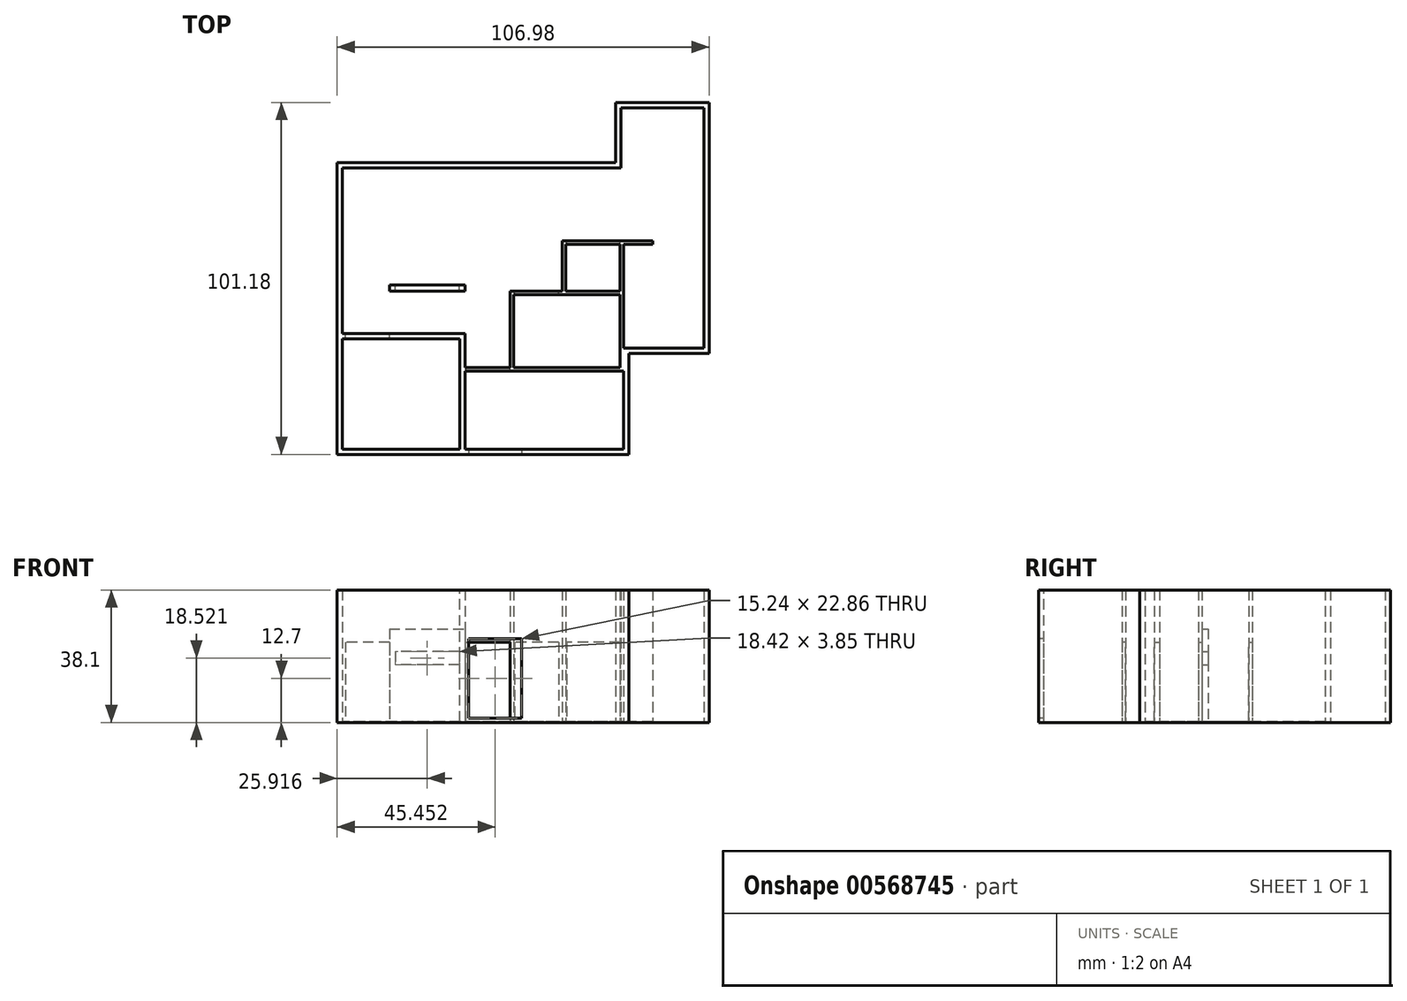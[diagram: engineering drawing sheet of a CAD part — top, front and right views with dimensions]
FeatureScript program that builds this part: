
annotation { "Feature Type Name" : "Feature", "Feature Type Description" : "" }
export const myFeature = defineFeature(function(context is Context, id is Id, definition is map)
    precondition{}
    {
        {
            var Q0;
            Q0=qCreatedBy(makeId("Top.planeOp"),FACE);
            var sketch = newSketch(context, id + "F0", { "sketchPlane" : qUnion([Q0])});
            skLineSegment(sketch, "E0.bottom", {"start": v(42.29, -41.97) * mm, "end": v(-41.64, -41.97) * mm});
            skLineSegment(sketch, "E0.top", {"start": v(42.29, 41.96) * mm, "end": v(-41.64, 41.96) * mm});
            skLineSegment(sketch, "E0.left", {"start": v(42.29, -41.97) * mm, "end": v(42.29, 41.96) * mm});
            skLineSegment(sketch, "E0.right", {"start": v(-41.64, -41.97) * mm, "end": v(-41.64, 41.96) * mm});
            skPoint(sketch, "E0.middle", {"position": v(0.32, 0) * mm});
            skLineSegment(sketch, "E1.MirrorCS", {"start": v(59.54, -38.2) * mm, "end": v(59.54, -65.02) * mm});
            skLineSegment(sketch, "E2.MirrorCS", {"start": v(-12.63, -38.2) * mm, "end": v(-12.63, -65.02) * mm});
            skPoint(sketch, "E3.MirrorP", {"position": v(-0.32, 0) * mm});
            skLineSegment(sketch, "E4.MirrorCS", {"start": v(-12.63, -65.02) * mm, "end": v(59.54, -65.02) * mm});
            skLineSegment(sketch, "E5.MirrorCS", {"start": v(-12.63, -38.2) * mm, "end": v(59.54, -38.2) * mm});
            skSolve(sketch);
        }
        {
            var Q0;
            {var subQ2=sQuery(id+"F0.wireOp",EDGE,"E0.top");Q0=makeQuery(id+"F0.imprint","IMPRINT",FACE,{"disambiguationData":[TD([[makeQuery(id+"F0.imprint","IMPRINT",EDGE,{"derivedFrom":subQ2}),1.0]])]});}
            var Q1;
            {var subQ0=sQuery(id+"F0.wireOp",EDGE,"E1.MirrorCS");Q1=makeQuery(id+"F0.imprint","IMPRINT",FACE,{"disambiguationData":[TD([[makeQuery(id+"F0.imprint","IMPRINT",EDGE,{"derivedFrom":subQ0}),-1.0]])]});}
            var Q2;
            {var subQ0=sQuery(id+"F0.wireOp",EDGE,"E0.left");var subQ1=sQuery(id+"F0.wireOp",EDGE,"E0.bottom");var subQ2=makeQuery(id+"F0.imprint","INTERSECT",VERTEX,{"derivedFrom":[subQ1,subQ0]});Q2=makeQuery(id+"F0.imprint","IMPRINT",FACE,{"disambiguationData":[TD([[makeQuery(id+"F0.imprint","IMPRINT",EDGE,{"disambiguationData":[TD([[subQ2,-1.0]])],"derivedFrom":subQ1}),-1.0]])]});}
            extrude(context, id + "F1", {"entities" : qUnion([Q0, Q1, Q2]), "depth" : 38.1 * mm, "offsetDistance" : 25.4 * mm});
        }
        {
            var Q0;
            Q0=makeQuery(id+"F1.opExtrude","CAP_FACE",FACE,{"disambiguationData":[OSD([sQuery(id+"F0.wireOp",EDGE,"E0.bottom"),sQuery(id+"F0.wireOp",EDGE,"E0.top"),sQuery(id+"F0.wireOp",EDGE,"E0.left"),sQuery(id+"F0.wireOp",EDGE,"E0.right"),sQuery(id+"F0.wireOp",EDGE,"E1.MirrorCS"),sQuery(id+"F0.wireOp",EDGE,"E2.MirrorCS"),sQuery(id+"F0.wireOp",EDGE,"E4.MirrorCS"),sQuery(id+"F0.wireOp",EDGE,"E5.MirrorCS")])],"isStart":false});
            shell(context, id + "F2", {"entities" : qUnion([Q0]), "thickness" : 1.52 * mm});
        }
        {
            var Q0;
            Q0=makeQuery(id+"F1.opExtrude","SWEPT_BODY",BODY,{"disambiguationData":[OSD([sQuery(id+"F0.wireOp",EDGE,"E0.bottom"),sQuery(id+"F0.wireOp",EDGE,"E0.top"),sQuery(id+"F0.wireOp",EDGE,"E0.left"),sQuery(id+"F0.wireOp",EDGE,"E0.right"),sQuery(id+"F0.wireOp",EDGE,"E1.MirrorCS"),sQuery(id+"F0.wireOp",EDGE,"E2.MirrorCS"),sQuery(id+"F0.wireOp",EDGE,"E4.MirrorCS"),sQuery(id+"F0.wireOp",EDGE,"E5.MirrorCS")])]});
            var Q1;
            Q1=makeQuery(id+"F1.opExtrude","SWEPT_EDGE",EDGE,{"disambiguationData":[OSD([sQuery(id+"F0.wireOp",EDGE,"E2.MirrorCS"),sQuery(id+"F0.wireOp",EDGE,"E4.MirrorCS")])]});
            transform(context, id + "F3", {"entities" : qUnion([Q0]), "transformType" : TransformType.ROTATION, "transformAxis" : qUnion([Q1]), "angle" : 270 * degree, "makeCopy" : false});
        }
        {
            var Q0;
            Q0=makeQuery(id+"F1.opExtrude","SWEPT_BODY",BODY,{"disambiguationData":[OSD([sQuery(id+"F0.wireOp",EDGE,"E0.bottom"),sQuery(id+"F0.wireOp",EDGE,"E0.top"),sQuery(id+"F0.wireOp",EDGE,"E0.left"),sQuery(id+"F0.wireOp",EDGE,"E0.right"),sQuery(id+"F0.wireOp",EDGE,"E1.MirrorCS"),sQuery(id+"F0.wireOp",EDGE,"E2.MirrorCS"),sQuery(id+"F0.wireOp",EDGE,"E4.MirrorCS"),sQuery(id+"F0.wireOp",EDGE,"E5.MirrorCS")])]});
            transform(context, id + "F4", {"entities" : qUnion([Q0]), "transformType" : TransformType.TRANSLATION_3D, "dx" : 77.47 * mm, "dy" : 55.37 * mm, "dz" : 0 * mm, "makeCopy" : false});
        }
        {
            var Q0;
            Q0=makeQuery(id+"F2.opShell","OFFSET_FACE",FACE,{"disambiguationData":[OSD([sQuery(id+"F0.wireOp",EDGE,"E0.bottom"),sQuery(id+"F0.wireOp",EDGE,"E0.top"),sQuery(id+"F0.wireOp",EDGE,"E0.left"),sQuery(id+"F0.wireOp",EDGE,"E0.right"),sQuery(id+"F0.wireOp",EDGE,"E1.MirrorCS"),sQuery(id+"F0.wireOp",EDGE,"E2.MirrorCS"),sQuery(id+"F0.wireOp",EDGE,"E4.MirrorCS"),sQuery(id+"F0.wireOp",EDGE,"E5.MirrorCS")])]});
            var sketch = newSketch(context, id + "F5", { "sketchPlane" : qUnion([Q0])});
            skLineSegment(sketch, "E6", {"start": v(40.26, 22.82) * mm, "end": v(40.26, -13.72) * mm});
            skLineSegment(sketch, "E7", {"start": v(43.34, 22.82) * mm, "end": v(40.26, 22.82) * mm});
            skLineSegment(sketch, "E8", {"start": v(38.23, -13.72) * mm, "end": v(-5.32, -13.72) * mm});
            skLineSegment(sketch, "E9", {"start": v(-8.67, -37.13) * mm, "end": v(-8.67, -8.13) * mm});
            skLineSegment(sketch, "E10", {"start": v(7.55, -13.72) * mm, "end": v(7.55, 8.33) * mm});
            skLineSegment(sketch, "E11", {"start": v(7.55, 8.33) * mm, "end": v(40.26, 8.33) * mm});
            skLineSegment(sketch, "E12", {"start": v(40.26, 22.82) * mm, "end": v(22.55, 22.82) * mm});
            skLineSegment(sketch, "E13", {"start": v(22.55, 22.82) * mm, "end": v(22.55, 8.33) * mm});
            skLineSegment(sketch, "E14", {"start": v(-5.32, -13.72) * mm, "end": v(-5.32, -3.92) * mm});
            skLineSegment(sketch, "E15", {"start": v(-5.32, -3.92) * mm, "end": v(-40.62, -3.92) * mm});
            skLineSegment(sketch, "E16", {"start": v(-30.23, 9.32) * mm, "end": v(-5.32, 9.32) * mm});
            skSolve(sketch);
        }
        {
            var Q0;
            {var subQ0=sQuery(id+"F5.wireOp",EDGE,"E12");Q0=makeQuery(id+"F5.imprint","IMPRINT",FACE,{"disambiguationData":[TD([[makeQuery(id+"F5.imprint","IMPRINT",EDGE,{"derivedFrom":subQ0}),1.0]])]});}
            var Q1;
            {var subQ6=sQuery(id+"F5.wireOp",EDGE,"E10");Q1=makeQuery(id+"F5.imprint","IMPRINT",FACE,{"disambiguationData":[TD([[makeQuery(id+"F5.imprint","IMPRINT",EDGE,{"derivedFrom":subQ6}),-1.0]])]});}
            var Q2;
            {var subQ1=sQuery(id+"F5.wireOp",EDGE,"E14");Q2=makeQuery(id+"F5.imprint","IMPRINT",FACE,{"disambiguationData":[TD([[makeQuery(id+"F5.imprint","IMPRINT",EDGE,{"derivedFrom":subQ1}),1.0]])]});}
            extrude(context, id + "F6", {"entities" : qUnion([Q0, Q1, Q2]), "operationType" : NewBodyOperationType.ADD, "depth" : 25.4 * mm, "offsetDistance" : 25.4 * mm});
        }
        {
            var Q0;
            Q0=makeQuery(id+"F6.opExtrude","CAP_FACE",FACE,{"disambiguationData":[OSD([sQuery(id+"F0.wireOp",EDGE,"E0.bottom"),sQuery(id+"F0.wireOp",EDGE,"E0.top"),sQuery(id+"F0.wireOp",EDGE,"E0.right"),sQuery(id+"F5.wireOp",EDGE,"E6"),sQuery(id+"F5.wireOp",EDGE,"E8"),sQuery(id+"F5.wireOp",EDGE,"E10"),sQuery(id+"F5.wireOp",EDGE,"E11"),sQuery(id+"F5.wireOp",EDGE,"E12"),sQuery(id+"F5.wireOp",EDGE,"E13"),sQuery(id+"F5.wireOp",EDGE,"E14"),sQuery(id+"F5.wireOp",EDGE,"E15")])],"isStart":false});
            shell(context, id + "F7", {"entities" : qUnion([Q0]), "thickness" : 1.02 * mm});
        }
        {
            var Q0;
            Q0=makeQuery(id+"F7.opShell","OFFSET_FACE",FACE,{"disambiguationData":[OSD([sQuery(id+"F0.wireOp",EDGE,"E0.bottom"),sQuery(id+"F0.wireOp",EDGE,"E0.top"),sQuery(id+"F0.wireOp",EDGE,"E0.left"),sQuery(id+"F0.wireOp",EDGE,"E0.right"),sQuery(id+"F0.wireOp",EDGE,"E1.MirrorCS"),sQuery(id+"F0.wireOp",EDGE,"E2.MirrorCS"),sQuery(id+"F0.wireOp",EDGE,"E4.MirrorCS"),sQuery(id+"F0.wireOp",EDGE,"E5.MirrorCS")])]});
            var sketch = newSketch(context, id + "F8", { "sketchPlane" : qUnion([Q0])});
            skLineSegment(sketch, "E17.bottom", {"start": v(-6.34, -14.74) * mm, "end": v(-5.32, -14.74) * mm});
            skLineSegment(sketch, "E17.top", {"start": v(-6.34, -37.64) * mm, "end": v(-5.32, -37.64) * mm});
            skLineSegment(sketch, "E17.left", {"start": v(-6.34, -14.74) * mm, "end": v(-6.34, -37.64) * mm});
            skLineSegment(sketch, "E17.right", {"start": v(-5.32, -14.74) * mm, "end": v(-5.32, -37.64) * mm});
            skLineSegment(sketch, "E18.bottom", {"start": v(8.56, -14.74) * mm, "end": v(40.26, -14.74) * mm});
            skLineSegment(sketch, "E18.top", {"start": v(8.56, -13.72) * mm, "end": v(40.26, -13.72) * mm});
            skLineSegment(sketch, "E18.left", {"start": v(8.56, -14.74) * mm, "end": v(8.56, -13.72) * mm});
            skLineSegment(sketch, "E18.right", {"start": v(40.26, -14.74) * mm, "end": v(40.26, -13.72) * mm});
            skLineSegment(sketch, "E19.bottom", {"start": v(23.56, 7.32) * mm, "end": v(39.25, 7.32) * mm});
            skLineSegment(sketch, "E19.top", {"start": v(23.56, 8.33) * mm, "end": v(39.25, 8.33) * mm});
            skLineSegment(sketch, "E19.left", {"start": v(23.56, 7.32) * mm, "end": v(23.56, 8.33) * mm});
            skLineSegment(sketch, "E19.right", {"start": v(39.25, 7.32) * mm, "end": v(39.25, 8.33) * mm});
            skLineSegment(sketch, "E20.bottom", {"start": v(40.26, 22.82) * mm, "end": v(48.56, 22.82) * mm});
            skLineSegment(sketch, "E20.top", {"start": v(40.26, 21.8) * mm, "end": v(48.56, 21.8) * mm});
            skLineSegment(sketch, "E20.left", {"start": v(40.26, 22.82) * mm, "end": v(40.26, 21.8) * mm});
            skLineSegment(sketch, "E20.right", {"start": v(48.56, 22.82) * mm, "end": v(48.56, 21.8) * mm});
            skLineSegment(sketch, "E21.bottom", {"start": v(40.26, -13.72) * mm, "end": v(39.25, -13.72) * mm});
            skLineSegment(sketch, "E21.top", {"start": v(40.26, -9.14) * mm, "end": v(39.25, -9.14) * mm});
            skLineSegment(sketch, "E21.left", {"start": v(40.26, -13.72) * mm, "end": v(40.26, -9.14) * mm});
            skLineSegment(sketch, "E21.right", {"start": v(39.25, -13.72) * mm, "end": v(39.25, -9.14) * mm});
            skSolve(sketch);
        }
        {
            var Q0;
            Q0=makeQuery(id+"F7.opShell","OFFSET_FACE",FACE,{"disambiguationData":[OSD([sQuery(id+"F0.wireOp",EDGE,"E0.bottom")])]});
            var Q1;
            Q1=makeQuery(id+"F2.opShell","OFFSET_FACE",FACE,{"disambiguationData":[OSD([sQuery(id+"F0.wireOp",EDGE,"E0.bottom")])]});
            extrude(context, id + "F9", {"entities" : qUnion([Q0]), "operationType" : NewBodyOperationType.ADD, "endBound" : BoundingType.UP_TO_SURFACE, "depth" : 25.4 * mm, "endBoundEntityFace" : qUnion([Q1]), "offsetDistance" : 25.4 * mm});
        }
        {
            var Q0;
            Q0=makeQuery(id+"F7.opShell","OFFSET_FACE",FACE,{"disambiguationData":[OSD([sQuery(id+"F0.wireOp",EDGE,"E0.right")])]});
            var Q1;
            Q1=makeQuery(id+"F2.opShell","OFFSET_FACE",FACE,{"disambiguationData":[OSD([sQuery(id+"F0.wireOp",EDGE,"E0.right")])]});
            extrude(context, id + "F10", {"entities" : qUnion([Q0]), "operationType" : NewBodyOperationType.ADD, "endBound" : BoundingType.UP_TO_SURFACE, "depth" : 25.4 * mm, "endBoundEntityFace" : qUnion([Q1]), "offsetDistance" : 25.4 * mm});
        }
        {
            var Q0;
            Q0=makeQuery(id+"F7.opShell","OFFSET_FACE",FACE,{"disambiguationData":[OSD([sQuery(id+"F0.wireOp",EDGE,"E0.top")])]});
            var Q1;
            Q1=makeQuery(id+"F2.opShell","OFFSET_FACE",FACE,{"disambiguationData":[OSD([sQuery(id+"F0.wireOp",EDGE,"E0.top")])]});
            extrude(context, id + "F11", {"entities" : qUnion([Q0]), "operationType" : NewBodyOperationType.ADD, "endBound" : BoundingType.UP_TO_SURFACE, "depth" : 25.4 * mm, "endBoundEntityFace" : qUnion([Q1]), "offsetDistance" : 25.4 * mm});
        }
        {
            var Q0;
            Q0 = qSketchRegion(id + "F8", true);
            var Q1;
            Q1=makeQuery(id+"F6.opExtrude","CAP_FACE",FACE,{"disambiguationData":[OSD([sQuery(id+"F0.wireOp",EDGE,"E0.bottom"),sQuery(id+"F0.wireOp",EDGE,"E0.top"),sQuery(id+"F0.wireOp",EDGE,"E0.right"),sQuery(id+"F5.wireOp",EDGE,"E6"),sQuery(id+"F5.wireOp",EDGE,"E8"),sQuery(id+"F5.wireOp",EDGE,"E10"),sQuery(id+"F5.wireOp",EDGE,"E11"),sQuery(id+"F5.wireOp",EDGE,"E12"),sQuery(id+"F5.wireOp",EDGE,"E13"),sQuery(id+"F5.wireOp",EDGE,"E14"),sQuery(id+"F5.wireOp",EDGE,"E15")])],"isStart":false});
            extrude(context, id + "F12", {"entities" : qUnion([Q0]), "operationType" : NewBodyOperationType.ADD, "endBound" : BoundingType.UP_TO_SURFACE, "depth" : 26.67 * mm, "endBoundEntityFace" : qUnion([Q1]), "offsetDistance" : 25.4 * mm});
        }
        {
            var Q0;
            Q0=makeQuery(id+"F7.opShell","OFFSET_FACE",FACE,{"disambiguationData":[OSD([sQuery(id+"F5.wireOp",EDGE,"E15")])]});
            extrude(context, id + "F13", {"entities" : qUnion([Q0]), "operationType" : NewBodyOperationType.ADD, "depth" : 0.5 * mm, "offsetDistance" : 25.4 * mm});
        }
        {
            var Q0;
            Q0=makeQuery(id+"F12.boolean.opBoolean","MERGE",FACE,{"derivedFrom":[makeQuery(id+"F7.opShell","OFFSET_FACE",FACE,{"disambiguationData":[OSD([sQuery(id+"F5.wireOp",EDGE,"E14")])]}),makeQuery(id+"F12.opExtrude","SWEPT_FACE",FACE,{"disambiguationData":[OSD([sQuery(id+"F8.wireOp",EDGE,"E17.left")])]})]});
            extrude(context, id + "F14", {"entities" : qUnion([Q0]), "operationType" : NewBodyOperationType.ADD, "depth" : 0.5 * mm, "offsetDistance" : 25.4 * mm});
        }
        {
            var Q0;
            Q0=makeQuery(id+"F1.opExtrude","SWEPT_FACE",FACE,{"disambiguationData":[OSD([sQuery(id+"F0.wireOp",EDGE,"E0.right")])]});
            var sketch = newSketch(context, id + "F15", { "sketchPlane" : qUnion([Q0])});
            skLineSegment(sketch, "E22.bottom", {"start": v(-4.3, 1.27) * mm, "end": v(10.93, 1.27) * mm});
            skLineSegment(sketch, "E22.top", {"start": v(-4.3, 24.13) * mm, "end": v(10.93, 24.13) * mm});
            skLineSegment(sketch, "E22.left", {"start": v(-4.3, 1.27) * mm, "end": v(-4.3, 24.13) * mm});
            skLineSegment(sketch, "E22.right", {"start": v(10.93, 1.27) * mm, "end": v(10.93, 24.13) * mm});
            skSolve(sketch);
        }
        {
            var Q0;
            Q0=makeQuery(id+"F15.imprint","IMPRINT",FACE,{"disambiguationData":[TD([[makeQuery(id+"F15.imprint","IMPRINT",EDGE,{"derivedFrom":sQuery(id+"F15.wireOp",EDGE,"E22.bottom")}),1.0]])]});
            extrude(context, id + "F16", {"entities" : qUnion([Q0]), "operationType" : NewBodyOperationType.REMOVE, "oppositeDirection" : true, "depth" : 2.54 * mm, "offsetDistance" : 25.4 * mm});
        }
        {
            var Q0;
            Q0=makeQuery(id+"F2.opShell","OFFSET_FACE",FACE,{"disambiguationData":[OSD([sQuery(id+"F0.wireOp",EDGE,"E0.bottom"),sQuery(id+"F0.wireOp",EDGE,"E0.top"),sQuery(id+"F0.wireOp",EDGE,"E0.left"),sQuery(id+"F0.wireOp",EDGE,"E0.right"),sQuery(id+"F0.wireOp",EDGE,"E1.MirrorCS"),sQuery(id+"F0.wireOp",EDGE,"E2.MirrorCS"),sQuery(id+"F0.wireOp",EDGE,"E4.MirrorCS"),sQuery(id+"F0.wireOp",EDGE,"E5.MirrorCS")])]});
            extrude(context, id + "F17", {"entities" : qUnion([Q0]), "operationType" : NewBodyOperationType.REMOVE, "oppositeDirection" : true, "depth" : 1.27 * mm, "offsetDistance" : 25.4 * mm});
        }
        {
            var Q0;
            {var subQ0=sQuery(id+"F5.wireOp",EDGE,"E11");Q0=makeQuery(id+"F17.boolean.opBoolean","MERGE",FACE,{"derivedFrom":[makeQuery(id+"F6.opExtrude","SWEPT_FACE",FACE,{"disambiguationData":[OSD([subQ0])]}),makeQuery(id+"F17.opExtrude","SWEPT_FACE",FACE,{"disambiguationData":[OSD([subQ0])]})]});}
            var sketch = newSketch(context, id + "F18", { "sketchPlane" : qUnion([Q0])});
            skLineSegment(sketch, "E23.bottom", {"start": v(-21.52, 23.11) * mm, "end": v(-8.82, 23.11) * mm});
            skLineSegment(sketch, "E23.top", {"start": v(-21.52, 0.25) * mm, "end": v(-8.82, 0.25) * mm});
            skLineSegment(sketch, "E23.left", {"start": v(-21.52, 23.11) * mm, "end": v(-21.52, 0.25) * mm});
            skLineSegment(sketch, "E23.right", {"start": v(-8.82, 23.11) * mm, "end": v(-8.82, 0.25) * mm});
            skSolve(sketch);
        }
        {
            var Q0;
            {var subQ0=sQuery(id+"F18.wireOp",EDGE,"E23.bottom");Q0=makeQuery(id+"F18.imprint","IMPRINT",FACE,{"disambiguationData":[TD([[makeQuery(id+"F18.imprint","IMPRINT",EDGE,{"derivedFrom":subQ0}),-1.0]])]});}
            extrude(context, id + "F19", {"entities" : qUnion([Q0]), "operationType" : NewBodyOperationType.REMOVE, "oppositeDirection" : true, "depth" : 1.27 * mm, "offsetDistance" : 25.4 * mm});
        }
        {
            var Q0;
            {var subQ0=sQuery(id+"F8.wireOp",EDGE,"E20.bottom");Q0=makeQuery(id+"F17.boolean.opBoolean","MERGE",FACE,{"derivedFrom":[makeQuery(id+"F12.boolean.opBoolean","MERGE",FACE,{"derivedFrom":[makeQuery(id+"F6.opExtrude","SWEPT_FACE",FACE,{"disambiguationData":[OSD([sQuery(id+"F5.wireOp",EDGE,"E12")])]}),makeQuery(id+"F12.opExtrude","SWEPT_FACE",FACE,{"disambiguationData":[OSD([subQ0])]})]})],"fromTools":[makeQuery(id+"F17.opExtrude","SWEPT_FACE",FACE,{"disambiguationData":[OSD([sQuery(id+"F0.wireOp",EDGE,"E0.bottom"),sQuery(id+"F0.wireOp",EDGE,"E0.top"),sQuery(id+"F0.wireOp",EDGE,"E0.left"),sQuery(id+"F0.wireOp",EDGE,"E0.right"),sQuery(id+"F0.wireOp",EDGE,"E1.MirrorCS"),sQuery(id+"F0.wireOp",EDGE,"E2.MirrorCS"),sQuery(id+"F0.wireOp",EDGE,"E4.MirrorCS"),sQuery(id+"F0.wireOp",EDGE,"E5.MirrorCS"),subQ0])]})]});}
            var sketch = newSketch(context, id + "F20", { "sketchPlane" : qUnion([Q0])});
            skLineSegment(sketch, "E24.bottom", {"start": v(-39.25, 23.11) * mm, "end": v(-23.82, 23.11) * mm});
            skLineSegment(sketch, "E24.top", {"start": v(-39.25, 0.25) * mm, "end": v(-23.82, 0.25) * mm});
            skLineSegment(sketch, "E24.left", {"start": v(-39.25, 23.11) * mm, "end": v(-39.25, 0.25) * mm});
            skLineSegment(sketch, "E24.right", {"start": v(-23.82, 23.11) * mm, "end": v(-23.82, 0.25) * mm});
            skSolve(sketch);
        }
        {
            var Q0;
            Q0=makeQuery(id+"F20.imprint","IMPRINT",FACE,{"disambiguationData":[TD([[makeQuery(id+"F20.imprint","IMPRINT",EDGE,{"derivedFrom":sQuery(id+"F20.wireOp",EDGE,"E24.bottom")}),-1.0]])]});
            extrude(context, id + "F21", {"entities" : qUnion([Q0]), "operationType" : NewBodyOperationType.REMOVE, "oppositeDirection" : true, "depth" : 1.27 * mm, "offsetDistance" : 25.4 * mm});
        }
        {
            var Q0;
            {var subQ0=sQuery(id+"F5.wireOp",EDGE,"E15");Q0=makeQuery(id+"F17.boolean.opBoolean","MERGE",FACE,{"derivedFrom":[makeQuery(id+"F6.opExtrude","SWEPT_FACE",FACE,{"disambiguationData":[OSD([subQ0])]}),makeQuery(id+"F17.opExtrude","SWEPT_FACE",FACE,{"disambiguationData":[OSD([subQ0])]})]});}
            var sketch = newSketch(context, id + "F22", { "sketchPlane" : qUnion([Q0])});
            skLineSegment(sketch, "E25.bottom", {"start": v(27.12, 23.11) * mm, "end": v(39.82, 23.11) * mm});
            skLineSegment(sketch, "E25.top", {"start": v(27.12, 0.25) * mm, "end": v(39.82, 0.25) * mm});
            skLineSegment(sketch, "E25.left", {"start": v(27.12, 23.11) * mm, "end": v(27.12, 0.25) * mm});
            skLineSegment(sketch, "E25.right", {"start": v(39.82, 23.11) * mm, "end": v(39.82, 0.25) * mm});
            skSolve(sketch);
        }
        {
            var Q0;
            {var subQ0=sQuery(id+"F22.wireOp",EDGE,"E25.left");Q0=makeQuery(id+"F22.imprint","IMPRINT",FACE,{"disambiguationData":[TD([[makeQuery(id+"F22.imprint","IMPRINT",EDGE,{"derivedFrom":subQ0}),1.0]])]});}
            extrude(context, id + "F23", {"entities" : qUnion([Q0]), "operationType" : NewBodyOperationType.REMOVE, "oppositeDirection" : true, "depth" : 1.78 * mm, "offsetDistance" : 25.4 * mm});
        }
        {
            var Q0;
            Q0=makeQuery(id+"F23.boolean.opBoolean","MERGE",FACE,{"derivedFrom":[makeQuery(id+"F21.boolean.opBoolean","MERGE",FACE,{"derivedFrom":[makeQuery(id+"F19.boolean.opBoolean","MERGE",FACE,{"derivedFrom":[makeQuery(id+"F17.boolean.opBoolean","COPY",FACE,{"derivedFrom":makeQuery(id+"F17.opExtrude","CAP_FACE",FACE,{"disambiguationData":[OSD([sQuery(id+"F0.wireOp",EDGE,"E0.bottom"),sQuery(id+"F0.wireOp",EDGE,"E0.top"),sQuery(id+"F0.wireOp",EDGE,"E0.left"),sQuery(id+"F0.wireOp",EDGE,"E0.right"),sQuery(id+"F0.wireOp",EDGE,"E1.MirrorCS"),sQuery(id+"F0.wireOp",EDGE,"E2.MirrorCS"),sQuery(id+"F0.wireOp",EDGE,"E4.MirrorCS"),sQuery(id+"F0.wireOp",EDGE,"E5.MirrorCS")])],"isStart":false})})],"fromTools":[makeQuery(id+"F19.opExtrude","SWEPT_FACE",FACE,{"disambiguationData":[OSD([sQuery(id+"F18.wireOp",EDGE,"E23.top")])]})]})],"fromTools":[makeQuery(id+"F21.opExtrude","SWEPT_FACE",FACE,{"disambiguationData":[OSD([sQuery(id+"F20.wireOp",EDGE,"E24.top")])]})]})],"fromTools":[makeQuery(id+"F23.opExtrude","SWEPT_FACE",FACE,{"disambiguationData":[OSD([sQuery(id+"F22.wireOp",EDGE,"E25.top")])]})]});
            var sketch = newSketch(context, id + "F24", { "sketchPlane" : qUnion([Q0])});
            skLineSegment(sketch, "E26.bottom", {"start": v(-27.12, 8.33) * mm, "end": v(-5.32, 8.33) * mm});
            skLineSegment(sketch, "E26.top", {"start": v(-27.12, 10.11) * mm, "end": v(-5.32, 10.11) * mm});
            skLineSegment(sketch, "E26.left", {"start": v(-27.12, 8.33) * mm, "end": v(-27.12, 10.11) * mm});
            skLineSegment(sketch, "E26.right", {"start": v(-5.32, 8.33) * mm, "end": v(-5.32, 10.11) * mm});
            skSolve(sketch);
        }
        {
            var Q0;
            Q0=makeQuery(id+"F24.imprint","IMPRINT",FACE,{"disambiguationData":[TD([[makeQuery(id+"F24.imprint","IMPRINT",EDGE,{"derivedFrom":sQuery(id+"F24.wireOp",EDGE,"E26.bottom")}),1.0]])]});
            var Q1;
            {var subQ0=sQuery(id+"F8.wireOp",EDGE,"E17.left");var subQ1=sQuery(id+"F5.wireOp",EDGE,"E14");var subQ2=sQuery(id+"F5.wireOp",EDGE,"E15");Q1=makeQuery(id+"F14.boolean.opBoolean","MERGE",FACE,{"derivedFrom":[makeQuery(id+"F13.boolean.opBoolean","MERGE",FACE,{"derivedFrom":[makeQuery(id+"F12.boolean.opBoolean","MERGE",FACE,{"derivedFrom":[makeQuery(id+"F6.opExtrude","CAP_FACE",FACE,{"disambiguationData":[OSD([sQuery(id+"F0.wireOp",EDGE,"E0.bottom"),sQuery(id+"F0.wireOp",EDGE,"E0.top"),sQuery(id+"F0.wireOp",EDGE,"E0.right"),sQuery(id+"F5.wireOp",EDGE,"E6"),sQuery(id+"F5.wireOp",EDGE,"E8"),sQuery(id+"F5.wireOp",EDGE,"E10"),sQuery(id+"F5.wireOp",EDGE,"E11"),sQuery(id+"F5.wireOp",EDGE,"E12"),sQuery(id+"F5.wireOp",EDGE,"E13"),subQ1,subQ2])],"isStart":false}),makeQuery(id+"F12.opExtrude","CAP_FACE",FACE,{"disambiguationData":[OSD([sQuery(id+"F8.wireOp",EDGE,"E17.bottom"),sQuery(id+"F8.wireOp",EDGE,"E17.top"),subQ0,sQuery(id+"F8.wireOp",EDGE,"E17.right")])],"isStart":false}),makeQuery(id+"F12.opExtrude","CAP_FACE",FACE,{"disambiguationData":[OSD([sQuery(id+"F8.wireOp",EDGE,"E18.bottom"),sQuery(id+"F8.wireOp",EDGE,"E18.top"),sQuery(id+"F8.wireOp",EDGE,"E18.left"),sQuery(id+"F8.wireOp",EDGE,"E18.right"),sQuery(id+"F8.wireOp",EDGE,"E21.bottom"),sQuery(id+"F8.wireOp",EDGE,"E21.top"),sQuery(id+"F8.wireOp",EDGE,"E21.left"),sQuery(id+"F8.wireOp",EDGE,"E21.right")])],"isStart":false}),makeQuery(id+"F12.opExtrude","CAP_FACE",FACE,{"disambiguationData":[OSD([sQuery(id+"F8.wireOp",EDGE,"E19.bottom"),sQuery(id+"F8.wireOp",EDGE,"E19.top"),sQuery(id+"F8.wireOp",EDGE,"E19.left"),sQuery(id+"F8.wireOp",EDGE,"E19.right")])],"isStart":false}),makeQuery(id+"F12.opExtrude","CAP_FACE",FACE,{"disambiguationData":[OSD([sQuery(id+"F8.wireOp",EDGE,"E20.bottom"),sQuery(id+"F8.wireOp",EDGE,"E20.top"),sQuery(id+"F8.wireOp",EDGE,"E20.left"),sQuery(id+"F8.wireOp",EDGE,"E20.right")])],"isStart":false})]}),makeQuery(id+"F13.opExtrude","SWEPT_FACE",FACE,{"disambiguationData":[OSD([subQ2])]})]}),makeQuery(id+"F14.opExtrude","SWEPT_FACE",FACE,{"disambiguationData":[OSD([subQ1,subQ0])]})]});}
            extrude(context, id + "F25", {"entities" : qUnion([Q0]), "operationType" : NewBodyOperationType.ADD, "endBound" : BoundingType.UP_TO_SURFACE, "depth" : 25.4 * mm, "endBoundEntityFace" : qUnion([Q1]), "offsetDistance" : 25.4 * mm});
        }
        {
            var Q0;
            Q0=makeQuery(id+"F25.opExtrude","SWEPT_FACE",FACE,{"disambiguationData":[OSD([sQuery(id+"F24.wireOp",EDGE,"E26.top")])]});
            var sketch = newSketch(context, id + "F26", { "sketchPlane" : qUnion([Q0])});
            skLineSegment(sketch, "E27.bottom", {"start": v(7.01, 20.45) * mm, "end": v(25.43, 20.45) * mm});
            skLineSegment(sketch, "E27.top", {"start": v(7.01, 16.6) * mm, "end": v(25.43, 16.6) * mm});
            skLineSegment(sketch, "E27.left", {"start": v(7.01, 20.45) * mm, "end": v(7.01, 16.6) * mm});
            skLineSegment(sketch, "E27.right", {"start": v(25.43, 20.45) * mm, "end": v(25.43, 16.6) * mm});
            skSolve(sketch);
        }
        {
            var Q0;
            Q0=makeQuery(id+"F26.imprint","IMPRINT",FACE,{"disambiguationData":[TD([[makeQuery(id+"F26.imprint","IMPRINT",EDGE,{"derivedFrom":sQuery(id+"F26.wireOp",EDGE,"E27.bottom")}),-1.0]])]});
            extrude(context, id + "F27", {"entities" : qUnion([Q0]), "operationType" : NewBodyOperationType.REMOVE, "oppositeDirection" : true, "depth" : 1.78 * mm, "offsetDistance" : 25.4 * mm});
        }
        {
            var Q0;
            Q0=makeQuery(id+"F12.boolean.opBoolean","MERGE",FACE,{"derivedFrom":[makeQuery(id+"F7.opShell","OFFSET_FACE",FACE,{"disambiguationData":[OSD([sQuery(id+"F5.wireOp",EDGE,"E8")])]}),makeQuery(id+"F12.opExtrude","SWEPT_FACE",FACE,{"disambiguationData":[OSD([sQuery(id+"F8.wireOp",EDGE,"E18.bottom")])]})]});
            var sketch = newSketch(context, id + "F28", { "sketchPlane" : qUnion([Q0])});
            skLineSegment(sketch, "E28.bottom", {"start": v(-5.15, 23.11) * mm, "end": v(7.55, 23.11) * mm});
            skLineSegment(sketch, "E28.top", {"start": v(-5.15, 0.25) * mm, "end": v(7.55, 0.25) * mm});
            skLineSegment(sketch, "E28.left", {"start": v(-5.15, 23.11) * mm, "end": v(-5.15, 0.25) * mm});
            skLineSegment(sketch, "E28.right", {"start": v(7.55, 23.11) * mm, "end": v(7.55, 0.25) * mm});
            skSolve(sketch);
        }
        {
            var Q0;
            Q0=makeQuery(id+"F28.imprint","IMPRINT",FACE,{"disambiguationData":[TD([[makeQuery(id+"F28.imprint","IMPRINT",EDGE,{"derivedFrom":sQuery(id+"F28.wireOp",EDGE,"E28.bottom")}),-1.0]])]});
            var Q1;
            {var subQ0=sQuery(id+"F5.wireOp",EDGE,"E8");Q1=makeQuery(id+"F17.boolean.opBoolean","MERGE",FACE,{"derivedFrom":[makeQuery(id+"F6.opExtrude","SWEPT_FACE",FACE,{"disambiguationData":[OSD([subQ0])]}),makeQuery(id+"F17.opExtrude","SWEPT_FACE",FACE,{"disambiguationData":[OSD([subQ0])]})]});}
            extrude(context, id + "F29", {"entities" : qUnion([Q0]), "operationType" : NewBodyOperationType.REMOVE, "endBound" : BoundingType.UP_TO_SURFACE, "oppositeDirection" : true, "depth" : 25.4 * mm, "endBoundEntityFace" : qUnion([Q1]), "offsetDistance" : 25.4 * mm});
        }
        {
            var Q0;
            {var subQ0=sQuery(id+"F8.wireOp",EDGE,"E17.left");var subQ1=sQuery(id+"F5.wireOp",EDGE,"E14");var subQ2=sQuery(id+"F5.wireOp",EDGE,"E15");Q0=makeQuery(id+"F14.boolean.opBoolean","MERGE",FACE,{"derivedFrom":[makeQuery(id+"F13.boolean.opBoolean","MERGE",FACE,{"derivedFrom":[makeQuery(id+"F12.boolean.opBoolean","MERGE",FACE,{"derivedFrom":[makeQuery(id+"F6.opExtrude","CAP_FACE",FACE,{"disambiguationData":[OSD([sQuery(id+"F0.wireOp",EDGE,"E0.bottom"),sQuery(id+"F0.wireOp",EDGE,"E0.top"),sQuery(id+"F0.wireOp",EDGE,"E0.right"),sQuery(id+"F5.wireOp",EDGE,"E6"),sQuery(id+"F5.wireOp",EDGE,"E8"),sQuery(id+"F5.wireOp",EDGE,"E10"),sQuery(id+"F5.wireOp",EDGE,"E11"),sQuery(id+"F5.wireOp",EDGE,"E12"),sQuery(id+"F5.wireOp",EDGE,"E13"),subQ1,subQ2])],"isStart":false}),makeQuery(id+"F12.opExtrude","CAP_FACE",FACE,{"disambiguationData":[OSD([sQuery(id+"F8.wireOp",EDGE,"E17.bottom"),sQuery(id+"F8.wireOp",EDGE,"E17.top"),subQ0,sQuery(id+"F8.wireOp",EDGE,"E17.right")])],"isStart":false}),makeQuery(id+"F12.opExtrude","CAP_FACE",FACE,{"disambiguationData":[OSD([sQuery(id+"F8.wireOp",EDGE,"E18.bottom"),sQuery(id+"F8.wireOp",EDGE,"E18.top"),sQuery(id+"F8.wireOp",EDGE,"E18.left"),sQuery(id+"F8.wireOp",EDGE,"E18.right"),sQuery(id+"F8.wireOp",EDGE,"E21.bottom"),sQuery(id+"F8.wireOp",EDGE,"E21.top"),sQuery(id+"F8.wireOp",EDGE,"E21.left"),sQuery(id+"F8.wireOp",EDGE,"E21.right")])],"isStart":false}),makeQuery(id+"F12.opExtrude","CAP_FACE",FACE,{"disambiguationData":[OSD([sQuery(id+"F8.wireOp",EDGE,"E19.bottom"),sQuery(id+"F8.wireOp",EDGE,"E19.top"),sQuery(id+"F8.wireOp",EDGE,"E19.left"),sQuery(id+"F8.wireOp",EDGE,"E19.right")])],"isStart":false}),makeQuery(id+"F12.opExtrude","CAP_FACE",FACE,{"disambiguationData":[OSD([sQuery(id+"F8.wireOp",EDGE,"E20.bottom"),sQuery(id+"F8.wireOp",EDGE,"E20.top"),sQuery(id+"F8.wireOp",EDGE,"E20.left"),sQuery(id+"F8.wireOp",EDGE,"E20.right")])],"isStart":false})]}),makeQuery(id+"F13.opExtrude","SWEPT_FACE",FACE,{"disambiguationData":[OSD([subQ2])]})]}),makeQuery(id+"F14.opExtrude","SWEPT_FACE",FACE,{"disambiguationData":[OSD([subQ1,subQ0])]})]});}
            var Q1;
            Q1=makeQuery(id+"F1.opExtrude","CAP_FACE",FACE,{"disambiguationData":[OSD([sQuery(id+"F0.wireOp",EDGE,"E0.bottom"),sQuery(id+"F0.wireOp",EDGE,"E0.top"),sQuery(id+"F0.wireOp",EDGE,"E0.left"),sQuery(id+"F0.wireOp",EDGE,"E0.right"),sQuery(id+"F0.wireOp",EDGE,"E1.MirrorCS"),sQuery(id+"F0.wireOp",EDGE,"E2.MirrorCS"),sQuery(id+"F0.wireOp",EDGE,"E4.MirrorCS"),sQuery(id+"F0.wireOp",EDGE,"E5.MirrorCS")])],"isStart":false});
            extrude(context, id + "F30", {"entities" : qUnion([Q0]), "operationType" : NewBodyOperationType.ADD, "endBound" : BoundingType.UP_TO_SURFACE, "depth" : 25.4 * mm, "endBoundEntityFace" : qUnion([Q1]), "offsetDistance" : 25.4 * mm});
        }
        {
            var Q0;
            {var subQ0=sQuery(id+"F8.wireOp",EDGE,"E18.right");Q0=makeQuery(id+"F30.boolean.opBoolean","MERGE",FACE,{"derivedFrom":[makeQuery(id+"F12.opExtrude","SWEPT_FACE",FACE,{"disambiguationData":[OSD([subQ0])]}),makeQuery(id+"F30.opExtrude","SWEPT_FACE",FACE,{"disambiguationData":[OSD([subQ0])]})]});}
            var Q1;
            {var subQ0=sQuery(id+"F0.wireOp",EDGE,"E0.bottom");Q1=makeQuery(id+"F9.boolean.opBoolean","MERGE",FACE,{"derivedFrom":[makeQuery(id+"F2.opShell","OFFSET_FACE",FACE,{"disambiguationData":[OSD([subQ0])]}),makeQuery(id+"F9.opExtrude","CAP_FACE",FACE,{"disambiguationData":[OSD([subQ0])],"isStart":false})]});}
            extrude(context, id + "F31", {"entities" : qUnion([Q0]), "operationType" : NewBodyOperationType.ADD, "endBound" : BoundingType.UP_TO_SURFACE, "depth" : 25.4 * mm, "endBoundEntityFace" : qUnion([Q1]), "offsetDistance" : 25.4 * mm});
        }
        {
            var Q0;
            {var subQ0=sQuery(id+"F8.wireOp",EDGE,"E18.bottom");var subQ1=sQuery(id+"F5.wireOp",EDGE,"E8");var subQ2=sQuery(id+"F0.wireOp",EDGE,"E5.MirrorCS");var subQ3=sQuery(id+"F0.wireOp",EDGE,"E4.MirrorCS");var subQ4=sQuery(id+"F0.wireOp",EDGE,"E2.MirrorCS");var subQ5=sQuery(id+"F0.wireOp",EDGE,"E1.MirrorCS");var subQ6=sQuery(id+"F0.wireOp",EDGE,"E0.right");var subQ7=sQuery(id+"F0.wireOp",EDGE,"E0.left");var subQ8=sQuery(id+"F0.wireOp",EDGE,"E0.top");var subQ9=sQuery(id+"F0.wireOp",EDGE,"E0.bottom");Q0=makeQuery(id+"F29.boolean.opBoolean","MERGE",FACE,{"derivedFrom":[makeQuery(id+"F12.boolean.opBoolean","SPLIT",FACE,{"disambiguationData":[TD([makeQuery(id+"F2.opShell","OFFSET_FACE",FACE,{"disambiguationData":[OSD([subQ9])]})])],"derivedFrom":makeQuery(id+"F7.opShell","OFFSET_FACE",FACE,{"disambiguationData":[OSD([subQ9,subQ8,subQ7,subQ6,subQ5,subQ4,subQ3,subQ2])]})})],"fromTools":[makeQuery(id+"F29.opExtrude","SWEPT_FACE",FACE,{"disambiguationData":[OSD([subQ9,subQ8,subQ7,subQ6,subQ5,subQ4,subQ3,subQ2,subQ1,subQ0])]})]});}
            var Q1;
            Q1=makeQuery(id+"F23.boolean.opBoolean","MERGE",FACE,{"derivedFrom":[makeQuery(id+"F21.boolean.opBoolean","MERGE",FACE,{"derivedFrom":[makeQuery(id+"F19.boolean.opBoolean","MERGE",FACE,{"derivedFrom":[makeQuery(id+"F17.boolean.opBoolean","COPY",FACE,{"derivedFrom":makeQuery(id+"F17.opExtrude","CAP_FACE",FACE,{"disambiguationData":[OSD([sQuery(id+"F0.wireOp",EDGE,"E0.bottom"),sQuery(id+"F0.wireOp",EDGE,"E0.top"),sQuery(id+"F0.wireOp",EDGE,"E0.left"),sQuery(id+"F0.wireOp",EDGE,"E0.right"),sQuery(id+"F0.wireOp",EDGE,"E1.MirrorCS"),sQuery(id+"F0.wireOp",EDGE,"E2.MirrorCS"),sQuery(id+"F0.wireOp",EDGE,"E4.MirrorCS"),sQuery(id+"F0.wireOp",EDGE,"E5.MirrorCS")])],"isStart":false})}),makeQuery(id+"F19.opExtrude","SWEPT_FACE",FACE,{"disambiguationData":[OSD([sQuery(id+"F18.wireOp",EDGE,"E23.top")])]})]}),makeQuery(id+"F21.opExtrude","SWEPT_FACE",FACE,{"disambiguationData":[OSD([sQuery(id+"F20.wireOp",EDGE,"E24.top")])]})]}),makeQuery(id+"F23.opExtrude","SWEPT_FACE",FACE,{"disambiguationData":[OSD([sQuery(id+"F22.wireOp",EDGE,"E25.top")])]})]});
            extrude(context, id + "F32", {"entities" : qUnion([Q0]), "operationType" : NewBodyOperationType.REMOVE, "endBound" : BoundingType.UP_TO_SURFACE, "oppositeDirection" : true, "depth" : 25.4 * mm, "endBoundEntityFace" : qUnion([Q1]), "offsetDistance" : 25.4 * mm});
        }
        {
            var Q0;
            {var subQ0=sQuery(id+"F0.wireOp",EDGE,"E0.bottom");Q0=makeQuery(id+"F12.boolean.opBoolean","SPLIT",FACE,{"disambiguationData":[TD([makeQuery(id+"F7.opShell","OFFSET_FACE",FACE,{"disambiguationData":[OSD([sQuery(id+"F5.wireOp",EDGE,"E10")])]})])],"derivedFrom":makeQuery(id+"F7.opShell","OFFSET_FACE",FACE,{"disambiguationData":[OSD([subQ0,sQuery(id+"F0.wireOp",EDGE,"E0.top"),sQuery(id+"F0.wireOp",EDGE,"E0.left"),sQuery(id+"F0.wireOp",EDGE,"E0.right"),sQuery(id+"F0.wireOp",EDGE,"E1.MirrorCS"),sQuery(id+"F0.wireOp",EDGE,"E2.MirrorCS"),sQuery(id+"F0.wireOp",EDGE,"E4.MirrorCS"),sQuery(id+"F0.wireOp",EDGE,"E5.MirrorCS")])]})});}
            var Q1;
            {var subQ0=sQuery(id+"F0.wireOp",EDGE,"E5.MirrorCS");var subQ1=sQuery(id+"F0.wireOp",EDGE,"E4.MirrorCS");var subQ2=sQuery(id+"F0.wireOp",EDGE,"E2.MirrorCS");var subQ3=sQuery(id+"F0.wireOp",EDGE,"E1.MirrorCS");var subQ4=sQuery(id+"F0.wireOp",EDGE,"E0.right");var subQ5=sQuery(id+"F0.wireOp",EDGE,"E0.left");var subQ6=sQuery(id+"F0.wireOp",EDGE,"E0.top");var subQ7=sQuery(id+"F0.wireOp",EDGE,"E0.bottom");Q1=makeQuery(id+"F32.boolean.opBoolean","MERGE",FACE,{"derivedFrom":[makeQuery(id+"F23.boolean.opBoolean","MERGE",FACE,{"derivedFrom":[makeQuery(id+"F21.boolean.opBoolean","MERGE",FACE,{"derivedFrom":[makeQuery(id+"F19.boolean.opBoolean","MERGE",FACE,{"derivedFrom":[makeQuery(id+"F17.boolean.opBoolean","COPY",FACE,{"derivedFrom":makeQuery(id+"F17.opExtrude","CAP_FACE",FACE,{"disambiguationData":[OSD([subQ7,subQ6,subQ5,subQ4,subQ3,subQ2,subQ1,subQ0])],"isStart":false})})],"fromTools":[makeQuery(id+"F19.opExtrude","SWEPT_FACE",FACE,{"disambiguationData":[OSD([sQuery(id+"F18.wireOp",EDGE,"E23.top")])]})]})],"fromTools":[makeQuery(id+"F21.opExtrude","SWEPT_FACE",FACE,{"disambiguationData":[OSD([sQuery(id+"F20.wireOp",EDGE,"E24.top")])]})]})],"fromTools":[makeQuery(id+"F23.opExtrude","SWEPT_FACE",FACE,{"disambiguationData":[OSD([sQuery(id+"F22.wireOp",EDGE,"E25.top")])]})]})],"fromTools":[makeQuery(id+"F32.opExtrude","CAP_FACE",FACE,{"disambiguationData":[OSD([subQ7,subQ6,subQ5,subQ4,subQ3,subQ2,subQ1,subQ0,sQuery(id+"F5.wireOp",EDGE,"E8"),sQuery(id+"F8.wireOp",EDGE,"E18.bottom")])],"isStart":false})]});}
            extrude(context, id + "F33", {"entities" : qUnion([Q0]), "operationType" : NewBodyOperationType.REMOVE, "endBound" : BoundingType.UP_TO_SURFACE, "oppositeDirection" : true, "depth" : 25.4 * mm, "endBoundEntityFace" : qUnion([Q1]), "offsetDistance" : 25.4 * mm});
        }
        {
            var Q0;
            {var subQ0=sQuery(id+"F0.wireOp",EDGE,"E0.top");var subQ1=sQuery(id+"F0.wireOp",EDGE,"E0.right");Q0=makeQuery(id+"F12.boolean.opBoolean","SPLIT",FACE,{"disambiguationData":[TD([makeQuery(id+"F2.opShell","OFFSET_FACE",FACE,{"disambiguationData":[OSD([subQ0])]})])],"derivedFrom":makeQuery(id+"F7.opShell","OFFSET_FACE",FACE,{"disambiguationData":[OSD([sQuery(id+"F0.wireOp",EDGE,"E0.bottom"),subQ0,sQuery(id+"F0.wireOp",EDGE,"E0.left"),subQ1,sQuery(id+"F0.wireOp",EDGE,"E1.MirrorCS"),sQuery(id+"F0.wireOp",EDGE,"E2.MirrorCS"),sQuery(id+"F0.wireOp",EDGE,"E4.MirrorCS"),sQuery(id+"F0.wireOp",EDGE,"E5.MirrorCS")])]})});}
            var Q1;
            {var subQ0=sQuery(id+"F0.wireOp",EDGE,"E0.bottom");Q1=makeQuery(id+"F12.boolean.opBoolean","SPLIT",FACE,{"disambiguationData":[TD([makeQuery(id+"F7.opShell","OFFSET_FACE",FACE,{"disambiguationData":[OSD([sQuery(id+"F5.wireOp",EDGE,"E12")])]})])],"derivedFrom":makeQuery(id+"F7.opShell","OFFSET_FACE",FACE,{"disambiguationData":[OSD([subQ0,sQuery(id+"F0.wireOp",EDGE,"E0.top"),sQuery(id+"F0.wireOp",EDGE,"E0.left"),sQuery(id+"F0.wireOp",EDGE,"E0.right"),sQuery(id+"F0.wireOp",EDGE,"E1.MirrorCS"),sQuery(id+"F0.wireOp",EDGE,"E2.MirrorCS"),sQuery(id+"F0.wireOp",EDGE,"E4.MirrorCS"),sQuery(id+"F0.wireOp",EDGE,"E5.MirrorCS")])]})});}
            var Q2;
            {var subQ0=sQuery(id+"F0.wireOp",EDGE,"E5.MirrorCS");var subQ1=sQuery(id+"F0.wireOp",EDGE,"E4.MirrorCS");var subQ2=sQuery(id+"F0.wireOp",EDGE,"E2.MirrorCS");var subQ3=sQuery(id+"F0.wireOp",EDGE,"E1.MirrorCS");var subQ4=sQuery(id+"F0.wireOp",EDGE,"E0.right");var subQ5=sQuery(id+"F0.wireOp",EDGE,"E0.left");var subQ6=sQuery(id+"F0.wireOp",EDGE,"E0.top");var subQ7=sQuery(id+"F0.wireOp",EDGE,"E0.bottom");Q2=makeQuery(id+"F33.boolean.opBoolean","MERGE",FACE,{"derivedFrom":[makeQuery(id+"F32.boolean.opBoolean","MERGE",FACE,{"derivedFrom":[makeQuery(id+"F23.boolean.opBoolean","MERGE",FACE,{"derivedFrom":[makeQuery(id+"F21.boolean.opBoolean","MERGE",FACE,{"derivedFrom":[makeQuery(id+"F19.boolean.opBoolean","MERGE",FACE,{"derivedFrom":[makeQuery(id+"F17.boolean.opBoolean","COPY",FACE,{"derivedFrom":makeQuery(id+"F17.opExtrude","CAP_FACE",FACE,{"disambiguationData":[OSD([subQ7,subQ6,subQ5,subQ4,subQ3,subQ2,subQ1,subQ0])],"isStart":false})})],"fromTools":[makeQuery(id+"F19.opExtrude","SWEPT_FACE",FACE,{"disambiguationData":[OSD([sQuery(id+"F18.wireOp",EDGE,"E23.top")])]})]})],"fromTools":[makeQuery(id+"F21.opExtrude","SWEPT_FACE",FACE,{"disambiguationData":[OSD([sQuery(id+"F20.wireOp",EDGE,"E24.top")])]})]})],"fromTools":[makeQuery(id+"F23.opExtrude","SWEPT_FACE",FACE,{"disambiguationData":[OSD([sQuery(id+"F22.wireOp",EDGE,"E25.top")])]})]})],"fromTools":[makeQuery(id+"F32.opExtrude","CAP_FACE",FACE,{"disambiguationData":[OSD([subQ7,subQ6,subQ5,subQ4,subQ3,subQ2,subQ1,subQ0,sQuery(id+"F5.wireOp",EDGE,"E8"),sQuery(id+"F8.wireOp",EDGE,"E18.bottom")])],"isStart":false})]})],"fromTools":[makeQuery(id+"F33.opExtrude","CAP_FACE",FACE,{"disambiguationData":[OSD([subQ7,subQ6,subQ5,subQ4,subQ3,subQ2,subQ1,subQ0])],"isStart":false})]});}
            extrude(context, id + "F34", {"entities" : qUnion([Q0, Q1]), "operationType" : NewBodyOperationType.REMOVE, "endBound" : BoundingType.UP_TO_SURFACE, "oppositeDirection" : true, "depth" : 25.4 * mm, "endBoundEntityFace" : qUnion([Q2]), "offsetDistance" : 25.4 * mm});
        }
        {
            var Q0;
            {var subQ0=sQuery(id+"F8.wireOp",EDGE,"E21.right");Q0=makeQuery(id+"F33.boolean.opBoolean","MERGE",FACE,{"derivedFrom":[makeQuery(id+"F30.boolean.opBoolean","MERGE",FACE,{"derivedFrom":[makeQuery(id+"F12.opExtrude","SWEPT_FACE",FACE,{"disambiguationData":[OSD([subQ0])]}),makeQuery(id+"F30.opExtrude","SWEPT_FACE",FACE,{"disambiguationData":[OSD([subQ0])]})]})],"fromTools":[makeQuery(id+"F33.opExtrude","SWEPT_FACE",FACE,{"disambiguationData":[OSD([subQ0])]})]});}
            var Q1;
            {var subQ0=sQuery(id+"F5.wireOp",EDGE,"E6");var subQ1=sQuery(id+"F0.wireOp",EDGE,"E5.MirrorCS");var subQ2=sQuery(id+"F0.wireOp",EDGE,"E4.MirrorCS");var subQ3=sQuery(id+"F0.wireOp",EDGE,"E2.MirrorCS");var subQ4=sQuery(id+"F0.wireOp",EDGE,"E1.MirrorCS");var subQ5=sQuery(id+"F0.wireOp",EDGE,"E0.right");var subQ6=sQuery(id+"F0.wireOp",EDGE,"E0.left");var subQ7=sQuery(id+"F0.wireOp",EDGE,"E0.top");var subQ8=sQuery(id+"F0.wireOp",EDGE,"E0.bottom");var subQ10=makeQuery(id+"F7.opShell","OFFSET_FACE",FACE,{"disambiguationData":[OSD([subQ8,subQ0])]});var subQ11=sQuery(id+"F5.wireOp",EDGE,"E11");var subQ12=makeQuery(id+"F7.opShell","OFFSET_FACE",FACE,{"disambiguationData":[OSD([subQ11])]});Q1=makeQuery(id+"F33.boolean.opBoolean","MERGE",FACE,{"derivedFrom":[makeQuery(id+"F30.boolean.opBoolean","MERGE",FACE,{"derivedFrom":[makeQuery(id+"F12.boolean.opBoolean","SPLIT",FACE,{"disambiguationData":[TD([subQ12])],"derivedFrom":subQ10}),makeQuery(id+"F30.opExtrude","SWEPT_FACE",FACE,{"disambiguationData":[OSD([subQ8,subQ0]),TDD([makeQuery(id+"F12.boolean.opBoolean","SPLIT",EDGE,{"disambiguationData":[TD([subQ12])],"derivedFrom":makeQuery(id+"F7.opShell","OFFSET_EDGE",EDGE,{"disambiguationData":[OSD([subQ8,subQ0]),TDD([makeQuery(id+"F6.boolean.opBoolean","SPLIT",EDGE,{"disambiguationData":[topologyDisambiguationEdgeConnected([makeQuery(id+"F6.opExtrude","SWEPT_FACE",FACE,{"disambiguationData":[OSD([subQ8,subQ0])]})])],"derivedFrom":makeQuery(id+"F6.opExtrude","CAP_EDGE",EDGE,{"disambiguationData":[OSD([subQ8,subQ0])],"isStart":false})})])]})})])]})]})],"fromTools":[makeQuery(id+"F33.opExtrude","SWEPT_FACE",FACE,{"disambiguationData":[OSD([subQ8,subQ7,subQ6,subQ5,subQ4,subQ3,subQ2,subQ1,subQ0])]})]});}
            extrude(context, id + "F35", {"entities" : qUnion([Q0]), "operationType" : NewBodyOperationType.REMOVE, "endBound" : BoundingType.UP_TO_SURFACE, "oppositeDirection" : true, "depth" : 25.4 * mm, "endBoundEntityFace" : qUnion([Q1]), "offsetDistance" : 25.4 * mm});
        }
    });
